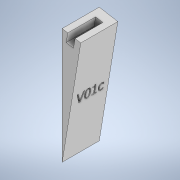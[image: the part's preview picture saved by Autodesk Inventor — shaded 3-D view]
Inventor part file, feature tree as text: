
AUTODESK INVENTOR PART (.ipt)
format: ipt  version: 2021.1 (Build 251245000, 245)  size: 208,896 bytes
history: native  units: in
note: dims shown in document units (in); Inventor stores cm internally (conversion verified against a paired STEP export)
features: extrude x3, sketch x3
ambient origin geometry x8: Origin, YZ Plane, XZ Plane, XY Plane, X Axis, Y Axis, Z Axis, Center Point
bodies: Solid1 (feature_tree)
feature tree (6):
  extrude  "Extrusion1"  Depth=1.0in TaperAngle=0.0deg
  extrude  "Extrusion4"  Depth=0.5in
  extrude  "Extrusion5"  Depth=0.2in
  sketch  "Sketch1"  dims[d0=3.125in d2=1.0in d3=0.0in]
  sketch  "Sketch4"  dims[d6=0.5497in d8=0.5in]
  sketch  "Sketch5"  dims[d11=0.1in d12=0.0in d13=0.2in d14=0.1539in d16=0.25in d17=0.75in d18=0.0in]
